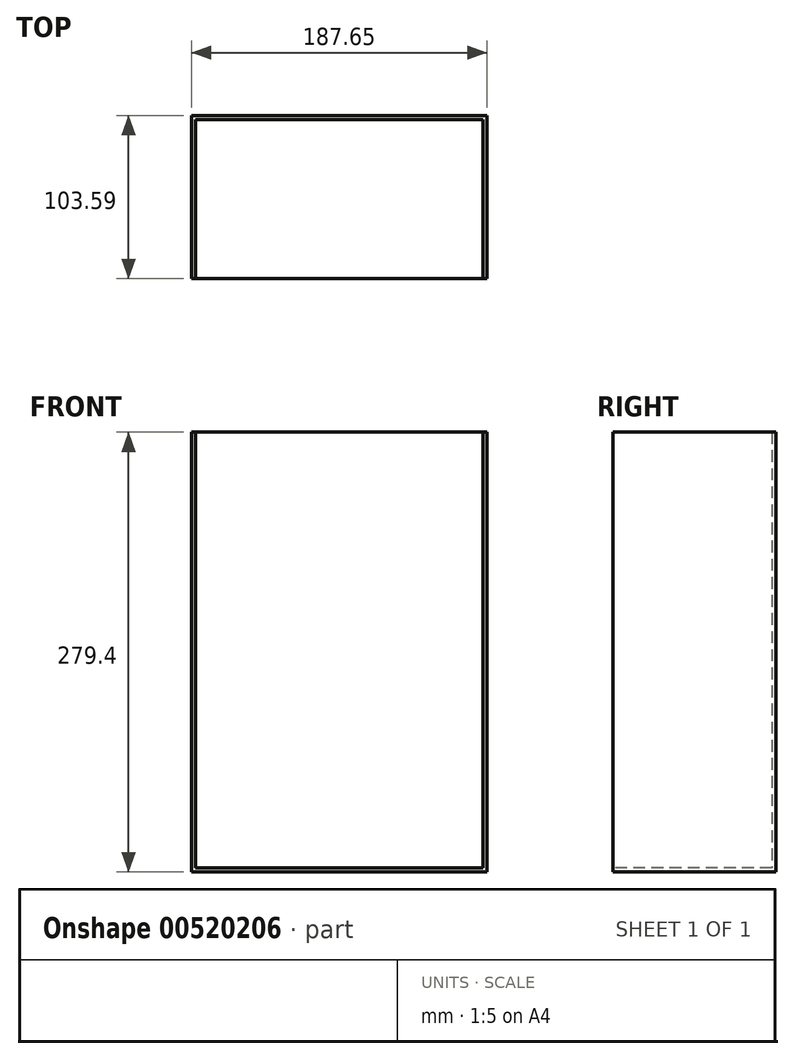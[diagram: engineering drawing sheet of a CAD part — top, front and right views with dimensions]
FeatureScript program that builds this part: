
annotation { "Feature Type Name" : "Feature", "Feature Type Description" : "" }
export const myFeature = defineFeature(function(context is Context, id is Id, definition is map)
    precondition{}
    {
        {
            var Q0;
            Q0=qCreatedBy(makeId("Top.planeOp"),FACE);
            var sketch = newSketch(context, id + "F0", { "sketchPlane" : qUnion([Q0])});
            skLineSegment(sketch, "E0.bottom", {"start": v(-120.9, 44.8) * mm, "end": v(66.76, 44.8) * mm});
            skLineSegment(sketch, "E0.top", {"start": v(-120.9, -58.78) * mm, "end": v(66.76, -58.78) * mm});
            skLineSegment(sketch, "E0.left", {"start": v(-120.9, 44.8) * mm, "end": v(-120.9, -58.78) * mm});
            skLineSegment(sketch, "E0.right", {"start": v(66.76, 44.8) * mm, "end": v(66.76, -58.78) * mm});
            skSolve(sketch);
        }
        {
            var Q0;
            Q0 = qSketchRegion(id + "F0", true);
            extrude(context, id + "F1", {"entities" : qUnion([Q0]), "depth" : 279.4 * mm, "offsetDistance" : 25.4 * mm});
        }
        {
            var Q0;
            Q0=makeQuery(id+"F1.opExtrude","SWEPT_FACE",FACE,{"disambiguationData":[OSD([sQuery(id+"F0.wireOp",EDGE,"E0.top")])]});
            var Q1;
            Q1=makeQuery(id+"F1.opExtrude","CAP_FACE",FACE,{"disambiguationData":[OSD([sQuery(id+"F0.wireOp",EDGE,"E0.bottom"),sQuery(id+"F0.wireOp",EDGE,"E0.top"),sQuery(id+"F0.wireOp",EDGE,"E0.left"),sQuery(id+"F0.wireOp",EDGE,"E0.right")])],"isStart":false});
            shell(context, id + "F2", {"entities" : qUnion([Q0, Q1]), "thickness" : 2.54 * mm});
        }
    });
